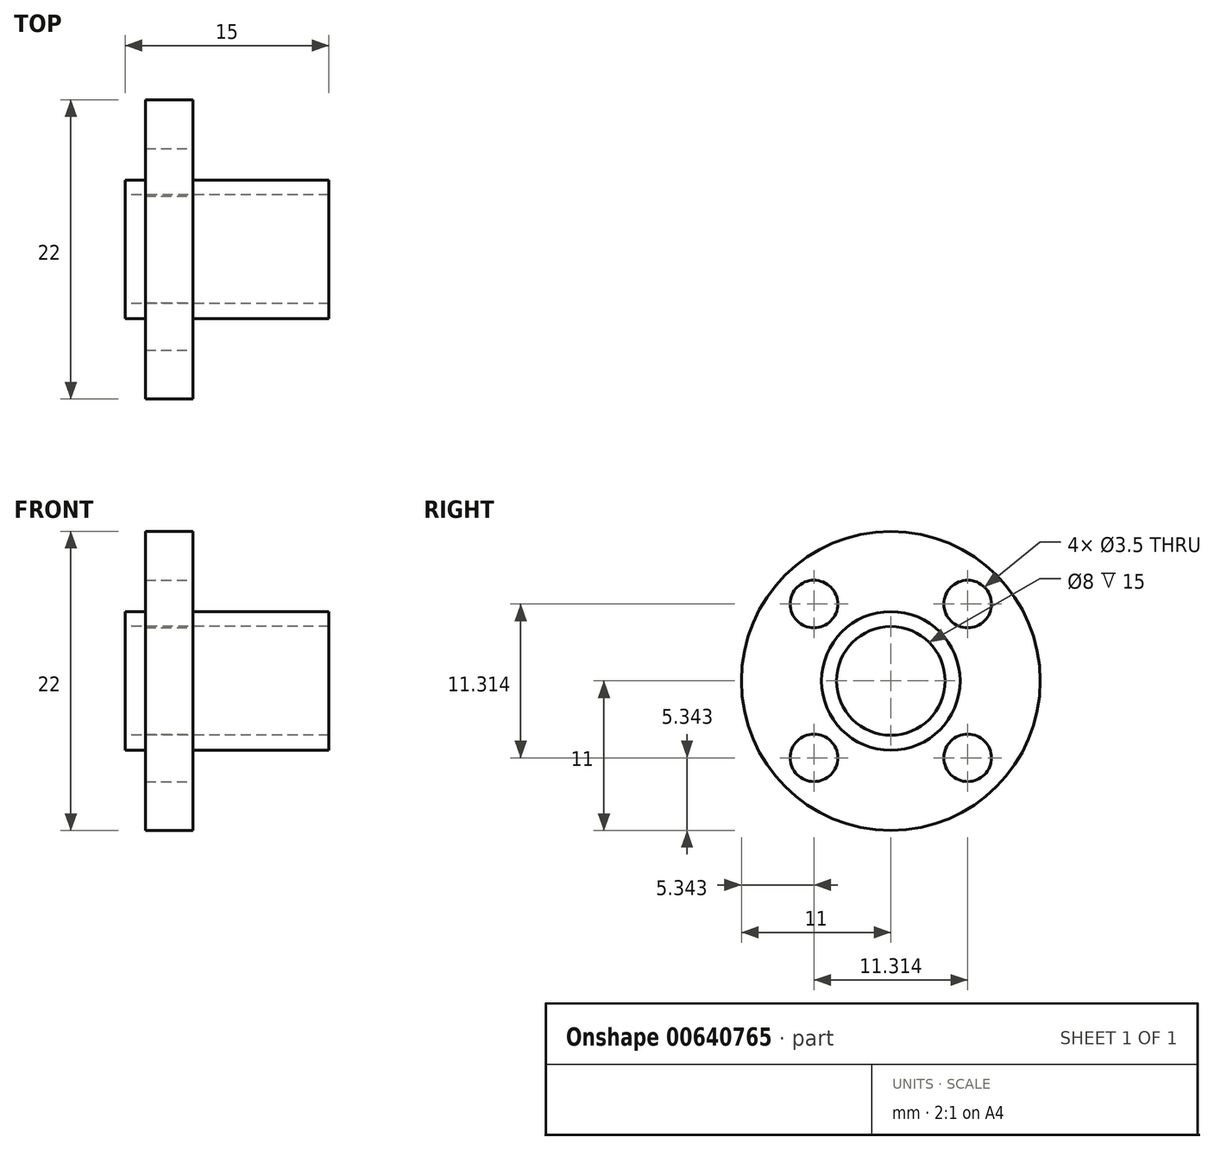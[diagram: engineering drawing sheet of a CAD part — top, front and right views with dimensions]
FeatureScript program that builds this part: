
annotation { "Feature Type Name" : "Feature", "Feature Type Description" : "" }
export const myFeature = defineFeature(function(context is Context, id is Id, definition is map)
    precondition{}
    {
        {
            var Q0;
            Q0=qCreatedBy(makeId("Top.planeOp"),FACE);
            var sketch = newSketch(context, id + "F0", { "sketchPlane" : qUnion([Q0])});
            skLineSegment(sketch, "E0", {"start": v(-2.95, 4) * mm, "end": v(12.05, 4) * mm});
            skLineSegment(sketch, "E1", {"start": v(12.05, 4) * mm, "end": v(12.05, 5.1) * mm});
            skLineSegment(sketch, "E2", {"start": v(12.05, 5.1) * mm, "end": v(2.05, 5.1) * mm});
            skLineSegment(sketch, "E3", {"start": v(2.05, 5.1) * mm, "end": v(2.05, 11) * mm});
            skLineSegment(sketch, "E4", {"start": v(2.05, 11) * mm, "end": v(-1.45, 11) * mm});
            skLineSegment(sketch, "E5", {"start": v(-1.45, 11) * mm, "end": v(-1.45, 5.1) * mm});
            skLineSegment(sketch, "E6", {"start": v(-1.45, 5.1) * mm, "end": v(-2.95, 5.1) * mm});
            skLineSegment(sketch, "E7", {"start": v(-2.95, 5.1) * mm, "end": v(-2.95, 4) * mm});
            skLineSegment(sketch, "E8", {"start": v(-2.95, 0) * mm, "end": v(12.05, 0) * mm, "construction": true});
            skLineSegment(sketch, "E9", {"start": v(12.05, 0) * mm, "end": v(12.05, 4) * mm, "construction": true});
            skLineSegment(sketch, "E10", {"start": v(-2.95, 4) * mm, "end": v(-2.95, 0) * mm, "construction": true});
            skSolve(sketch);
        }
        {
            var Q0;
            Q0=makeQuery(id+"F0.imprint","IMPRINT",FACE,{"disambiguationData":[TD([[makeQuery(id+"F0.imprint","IMPRINT",EDGE,{"derivedFrom":sQuery(id+"F0.wireOp",EDGE,"E0")}),1.0]])]});
            var Q1;
            Q1=sQuery(id+"F0.wireOp",EDGE,"E8");
            revolve(context, id + "F1", {"entities" : qUnion([Q0]), "axis" : qUnion([Q1]), "revolveType" : RevolveType.FULL});
        }
        {
            var Q0;
            Q0=qCreatedBy(makeId("Right.planeOp"),FACE);
            var sketch = newSketch(context, id + "F2", { "sketchPlane" : qUnion([Q0])});
            skCircle(sketch, "E11", {"center": v(-5.66, 5.66) * mm, "radius": 1.75 * mm});
            skCircle(sketch, "E12", {"center": v(5.66, 5.66) * mm, "radius": 1.75 * mm});
            skCircle(sketch, "E13", {"center": v(5.66, -5.66) * mm, "radius": 1.75 * mm});
            skCircle(sketch, "E14", {"center": v(-5.66, -5.66) * mm, "radius": 1.75 * mm});
            skLineSegment(sketch, "E15", {"start": v(-5.66, 5.66) * mm, "end": v(0, 0) * mm, "construction": true});
            skLineSegment(sketch, "E16", {"start": v(0, 0) * mm, "end": v(5.66, 5.66) * mm, "construction": true});
            skLineSegment(sketch, "E17", {"start": v(-5.66, -5.66) * mm, "end": v(0, 0) * mm, "construction": true});
            skLineSegment(sketch, "E18", {"start": v(5.66, -5.66) * mm, "end": v(0, 0) * mm, "construction": true});
            skSolve(sketch);
        }
        {
            var Q0;
            Q0 = qSketchRegion(id + "F2", true);
            extrude(context, id + "F3", {"entities" : qUnion([Q0]), "operationType" : NewBodyOperationType.REMOVE, "endBound" : BoundingType.SYMMETRIC, "oppositeDirection" : true, "depth" : 25 * mm, "offsetDistance" : 25 * mm});
        }
    });
